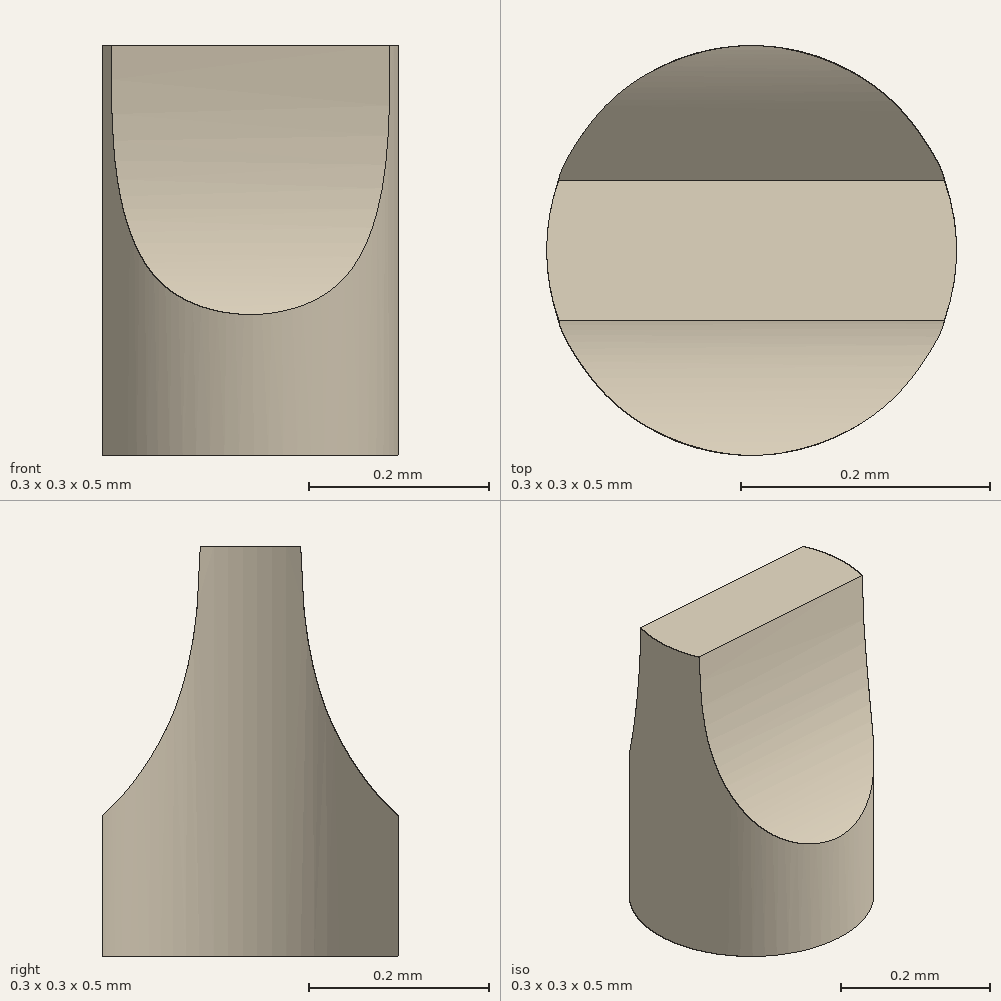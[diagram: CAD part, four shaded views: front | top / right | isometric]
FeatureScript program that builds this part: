
annotation { "Feature Type Name" : "Feature", "Feature Type Description" : "" }
export const myFeature = defineFeature(function(context is Context, id is Id, definition is map)
    precondition{}
    {
        {
            var Q0;
            Q0=qCreatedBy(makeId("Right.planeOp"),FACE);
            var sketch = newSketch(context, id + "F0", { "sketchPlane" : qUnion([Q0])});
            skLineSegment(sketch, "E0.bottom", {"start": v(0, 0) * mm, "end": v(0.17, 0) * mm});
            skLineSegment(sketch, "E0.top", {"start": v(0, 0.46) * mm, "end": v(0.17, 0.46) * mm});
            skLineSegment(sketch, "E0.left", {"start": v(0, 0) * mm, "end": v(0, 0.46) * mm});
            skLineSegment(sketch, "E0.right", {"start": v(0.17, 0) * mm, "end": v(0.17, 0.46) * mm});
            skSolve(sketch);
        }
        {
            var Q0;
            Q0=makeQuery(id+"F0.imprint","IMPRINT",FACE,{"disambiguationData":[TD([[makeQuery(id+"F0.imprint","IMPRINT",EDGE,{"derivedFrom":sQuery(id+"F0.wireOp",EDGE,"E0.bottom")}),1.0]])]});
            var Q1;
            Q1=sQuery(id+"F0.wireOp",EDGE,"E0.left");
            revolve(context, id + "F1", {"entities" : qUnion([Q0]), "axis" : qUnion([Q1]), "revolveType" : RevolveType.FULL});
        }
        {
            var Q0;
            Q0=qCreatedBy(makeId("Right.planeOp"),FACE);
            var sketch = newSketch(context, id + "F2", { "sketchPlane" : qUnion([Q0])});
            skFitSpline(sketch, "E1", {"points": [v(0.06, 0.47) * mm, v(0.2, 0.13) * mm], "startDerivative": vector(0, -0.53) * mm, "endDerivative": vector(0.31, -0.22) * mm});
            skLineSegment(sketch, "E2", {"start": v(0.2, 0.13) * mm, "end": v(0.38, 0) * mm, "construction": true});
            skLineSegment(sketch, "E3", {"start": v(0.2, 0.13) * mm, "end": v(0.2, 0.47) * mm});
            skLineSegment(sketch, "E4", {"start": v(0.2, 0.47) * mm, "end": v(0.06, 0.47) * mm});
            skFitSpline(sketch, "E5.MirrorCS", {"points": [v(-0.06, 0.47) * mm, v(-0.2, 0.13) * mm], "startDerivative": vector(0, -0.53) * mm, "endDerivative": vector(-0.31, -0.22) * mm});
            skLineSegment(sketch, "E6.MirrorCS", {"start": v(-0.2, 0.13) * mm, "end": v(-0.2, 0.47) * mm});
            skLineSegment(sketch, "E7.MirrorCS", {"start": v(-0.2, 0.47) * mm, "end": v(-0.06, 0.47) * mm});
            skSolve(sketch);
        }
        {
            var Q0;
            Q0=makeQuery(id+"F2.imprint","IMPRINT",FACE,{"disambiguationData":[TD([[makeQuery(id+"F2.imprint","IMPRINT",EDGE,{"derivedFrom":sQuery(id+"F2.wireOp",EDGE,"E5.MirrorCS")}),-1.0]])]});
            var Q1;
            Q1=makeQuery(id+"F2.imprint","IMPRINT",FACE,{"disambiguationData":[TD([[makeQuery(id+"F2.imprint","IMPRINT",EDGE,{"derivedFrom":sQuery(id+"F2.wireOp",EDGE,"E1")}),1.0]])]});
            extrude(context, id + "F3", {"entities" : qUnion([Q0, Q1]), "operationType" : NewBodyOperationType.REMOVE, "endBound" : BoundingType.SYMMETRIC, "oppositeDirection" : true, "depth" : 0.5 * mm});
        }
    });
